# Revit family: Aluminiumleergehäuse,mit beschichtbarer Oberfläche- Mx 161008 CR3
name_source: partatom
category: Generic Models
revit_build: Autodesk Revit 2017 (Build: 20190508_0315(x64)
units: mm (PartAtom-declared; Revit-internal decimal feet)

## family parameters
Always vertical = Yes
Can host rebar = No
Cut with Voids When Loaded = No
Part Type = Normal
Room Calculation Point = No
Round Connector Dimension = Use Diameter
Shared = No
Work Plane-Based = No

## types (1)
- Mx 161008 CR3
    Article Type = Mx 161008 CR3
    GTIN = 4012196622665
    Height = 81 mm  [stored 0.265748 ft]
    Length = 160 mm  [stored 0.524934 ft]
    Manufacturer = OBO Bettermann
    Manufacturer Art.No. = 2011389
    Material = Cast aluminium
    URL = http://www.obo-bettermann.com
    Width = 100 mm  [stored 0.328084 ft]
    Width 1 = 50 mm  [stored 0.164042 ft]

note: [stored X ft] marks values corroborated as IEEE doubles in the binary element streams (Revit-internal decimal feet)

## geometry (parser evidence)
native form markers: Sweep x3
no freeform markers — native parametric forms only
